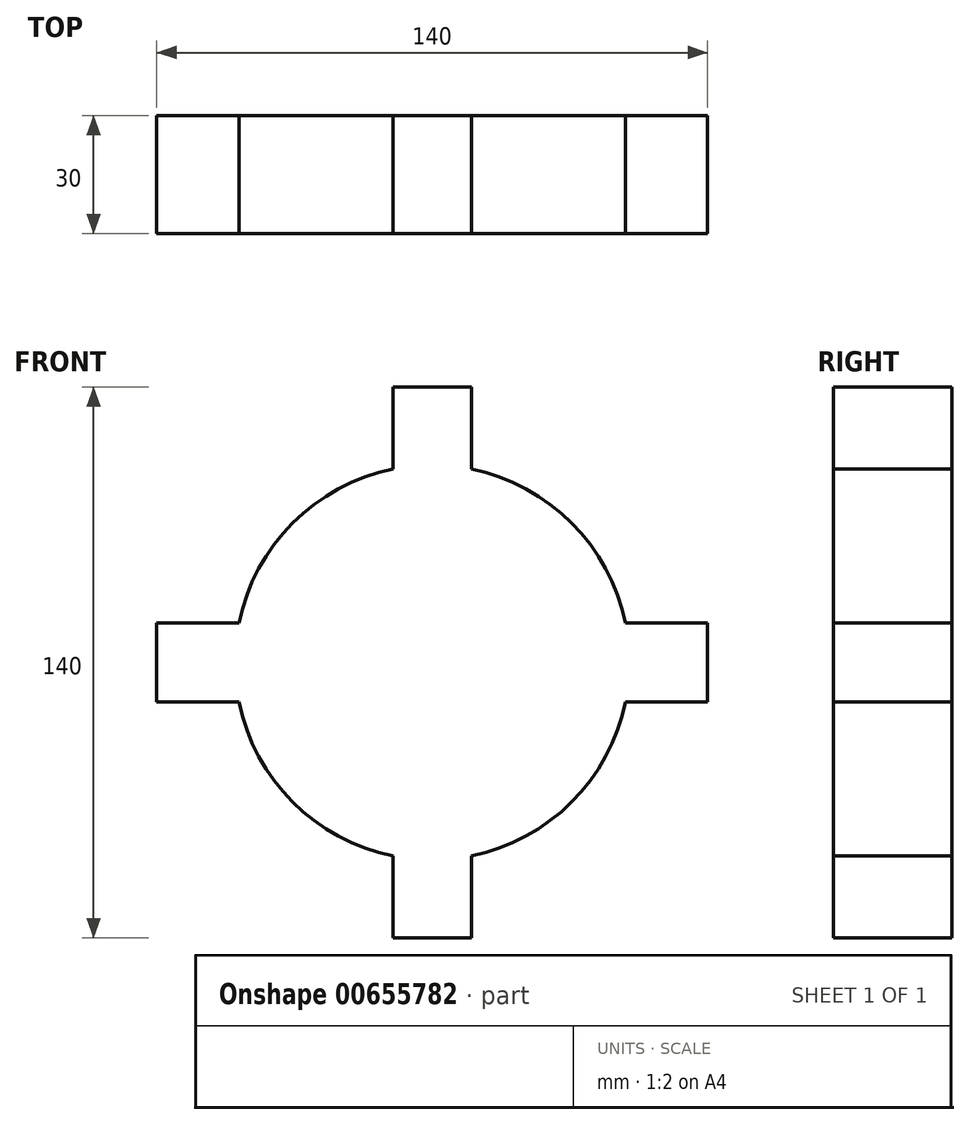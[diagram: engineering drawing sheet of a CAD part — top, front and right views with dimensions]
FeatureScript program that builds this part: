
annotation { "Feature Type Name" : "Feature", "Feature Type Description" : "" }
export const myFeature = defineFeature(function(context is Context, id is Id, definition is map)
    precondition{}
    {
        {
            var Q0;
            Q0=qCreatedBy(makeId("Front.planeOp"),FACE);
            var sketch = newSketch(context, id + "F0", { "sketchPlane" : qUnion([Q0])});
            skCircle(sketch, "E0", {"center": v(0, 0) * mm, "radius": 40 * mm});
            skLineSegment(sketch, "E1", {"start": v(0, 0) * mm, "end": v(-5.96, 0) * mm});
            skLineSegment(sketch, "E2", {"start": v(0, 0) * mm, "end": v(5.96, 0) * mm});
            skLineSegment(sketch, "E3", {"start": v(-10, 70) * mm, "end": v(5.96, 70) * mm});
            skLineSegment(sketch, "E4.MirrorCS", {"start": v(10, 70) * mm, "end": v(-5.96, 70) * mm});
            skLineSegment(sketch, "E5.MirrorCS", {"start": v(0, 0) * mm, "end": v(10, 0) * mm});
            skLineSegment(sketch, "E6", {"start": v(49.11, 10) * mm, "end": v(70, 10) * mm});
            skLineSegment(sketch, "E7", {"start": v(70, 10) * mm, "end": v(70, -10) * mm});
            skLineSegment(sketch, "E8.MirrorCS", {"start": v(10, -49.11) * mm, "end": v(10, -70) * mm});
            skLineSegment(sketch, "E9", {"start": v(-10, -70) * mm, "end": v(10, -70) * mm});
            skLineSegment(sketch, "E10.MirrorCS", {"start": v(-70, 10) * mm, "end": v(-70, -10) * mm});
            skCircle(sketch, "E11", {"center": v(0, 0) * mm, "radius": 50.12 * mm});
            skLineSegment(sketch, "E12.trimOffspring", {"start": v(-49.11, 10) * mm, "end": v(-70, 10) * mm});
            skLineSegment(sketch, "E13.trimOffspring", {"start": v(-49.11, -10) * mm, "end": v(-70, -10) * mm});
            skLineSegment(sketch, "E14.trimOffspring", {"start": v(-10, 49.11) * mm, "end": v(-10, 70) * mm});
            skLineSegment(sketch, "E15.trimOffspring", {"start": v(10, 49.11) * mm, "end": v(10, 70) * mm});
            skLineSegment(sketch, "E16.trimOffspring", {"start": v(49.11, -10) * mm, "end": v(70, -10) * mm});
            skPoint(sketch, "E17.orphan", {"position": v(10, 0) * mm});
            skLineSegment(sketch, "E18.trimOffspring", {"start": v(-10, -49.11) * mm, "end": v(-10, -70) * mm});
            skPoint(sketch, "E19.end.orphan", {"position": v(0, -10) * mm});
            skPoint(sketch, "E20.MirrorCS.end.orphan", {"position": v(0, 10) * mm});
            skPoint(sketch, "E21.orphan", {"position": v(-10, 0) * mm});
            skSolve(sketch);
        }
        {
            var Q0;
            {var subQ0=sQuery(id+"F0.wireOp",EDGE,"E6");Q0=makeQuery(id+"F0.imprint","IMPRINT",FACE,{"disambiguationData":[TD([[makeQuery(id+"F0.imprint","IMPRINT",EDGE,{"derivedFrom":subQ0}),-1.0]])]});}
            var Q1;
            Q1=makeQuery(id+"F0.imprint","IMPRINT",FACE,{"disambiguationData":[TD([[makeQuery(id+"F0.imprint","IMPRINT",EDGE,{"derivedFrom":sQuery(id+"F0.wireOp",EDGE,"E0")}),-1.0]])]});
            var Q2;
            Q2=makeQuery(id+"F0.imprint","IMPRINT",FACE,{"disambiguationData":[TD([[makeQuery(id+"F0.imprint","IMPRINT",EDGE,{"derivedFrom":sQuery(id+"F0.wireOp",EDGE,"E10.MirrorCS")}),1.0]])]});
            var Q3;
            {var subQ0=sQuery(id+"F0.wireOp",EDGE,"E8.MirrorCS");Q3=makeQuery(id+"F0.imprint","IMPRINT",FACE,{"disambiguationData":[TD([[makeQuery(id+"F0.imprint","IMPRINT",EDGE,{"derivedFrom":subQ0}),-1.0]])]});}
            var Q4;
            {var subQ4=sQuery(id+"F0.wireOp",EDGE,"E4.MirrorCS");Q4=makeQuery(id+"F0.imprint","IMPRINT",FACE,{"disambiguationData":[TD([[makeQuery(id+"F0.imprint","IMPRINT",EDGE,{"derivedFrom":subQ4}),1.0]])]});}
            var Q5;
            Q5=makeQuery(id+"F0.imprint","IMPRINT",FACE,{"disambiguationData":[TD([[makeQuery(id+"F0.imprint","IMPRINT",EDGE,{"derivedFrom":sQuery(id+"F0.wireOp",EDGE,"E0")}),1.0]])]});
            extrude(context, id + "F1", {"entities" : qUnion([Q0, Q1, Q2, Q3, Q4, Q5]), "depth" : 30 * mm, "offsetDistance" : 25 * mm});
        }
    });
